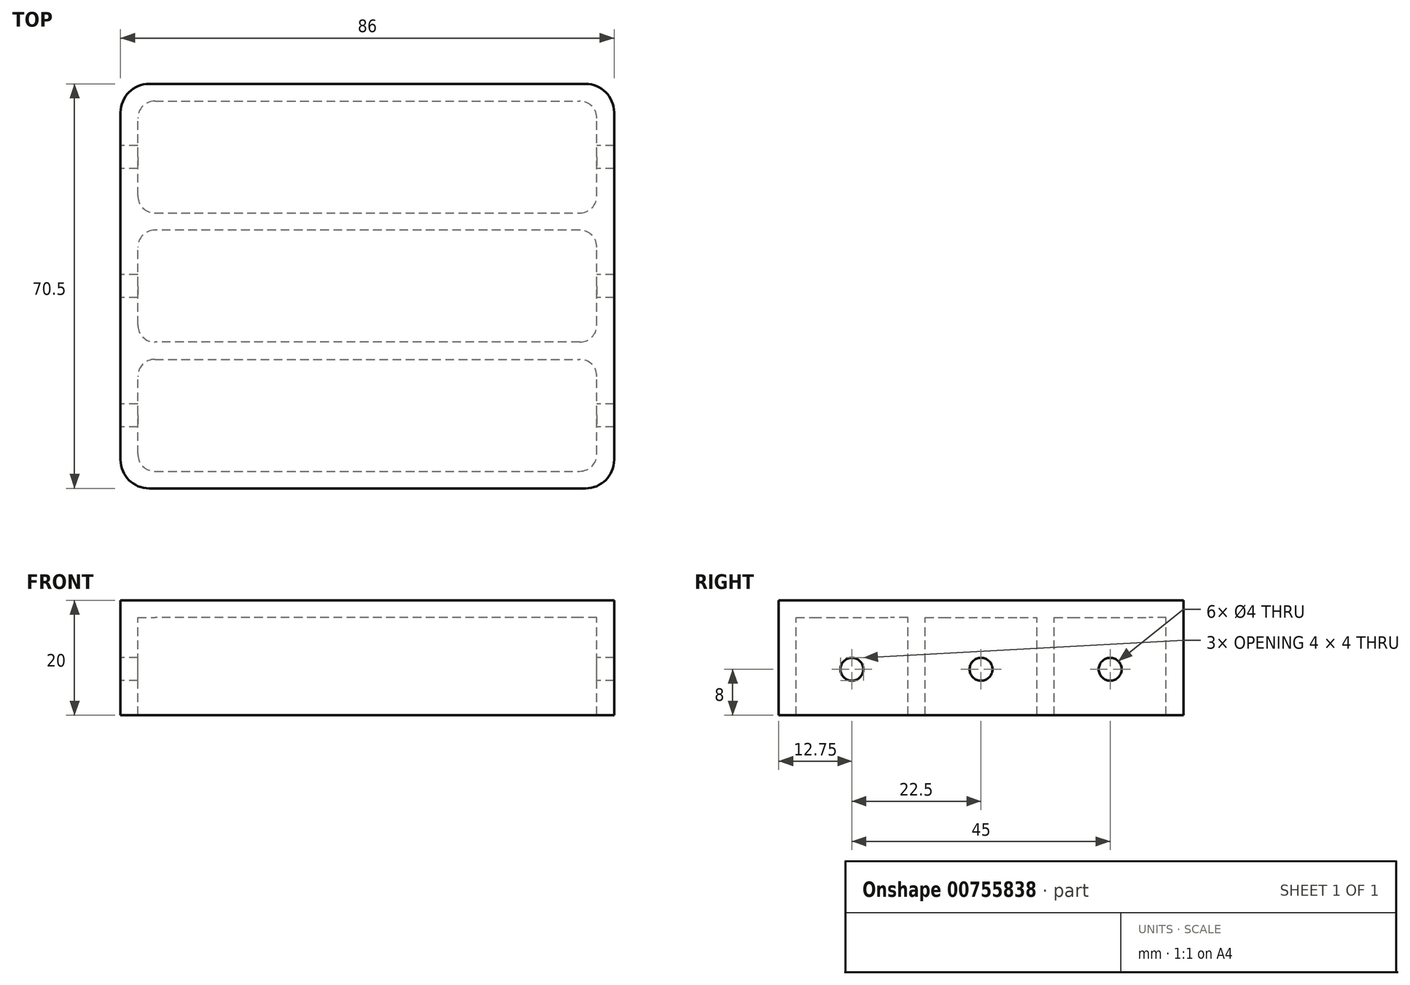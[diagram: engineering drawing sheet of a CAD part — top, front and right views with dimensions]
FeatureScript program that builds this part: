
annotation { "Feature Type Name" : "Feature", "Feature Type Description" : "" }
export const myFeature = defineFeature(function(context is Context, id is Id, definition is map)
    precondition{}
    {
        {
            var Q0;
            Q0=qCreatedBy(makeId("Top.planeOp"),FACE);
            var sketch = newSketch(context, id + "F0", { "sketchPlane" : qUnion([Q0])});
            skLineSegment(sketch, "E0.bottom", {"start": v(43, -35.25) * mm, "end": v(-43, -35.25) * mm});
            skLineSegment(sketch, "E0.top", {"start": v(43, 35.25) * mm, "end": v(-43, 35.25) * mm});
            skLineSegment(sketch, "E0.left", {"start": v(43, -35.25) * mm, "end": v(43, 35.25) * mm});
            skLineSegment(sketch, "E0.right", {"start": v(-43, -35.25) * mm, "end": v(-43, 35.25) * mm});
            skPoint(sketch, "E0.middle", {"position": v(0, 0) * mm});
            skLineSegment(sketch, "E1.bottom", {"start": v(40, -9.75) * mm, "end": v(-40, -9.75) * mm});
            skLineSegment(sketch, "E1.top", {"start": v(40, 9.75) * mm, "end": v(-40, 9.75) * mm});
            skLineSegment(sketch, "E1.left", {"start": v(40, -9.75) * mm, "end": v(40, 9.75) * mm});
            skLineSegment(sketch, "E1.right", {"start": v(-40, -9.75) * mm, "end": v(-40, 9.75) * mm});
            skLineSegment(sketch, "E2.bottom", {"start": v(-40, 12.75) * mm, "end": v(40, 12.75) * mm});
            skLineSegment(sketch, "E2.top", {"start": v(-40, 32.25) * mm, "end": v(40, 32.25) * mm});
            skLineSegment(sketch, "E2.left", {"start": v(-40, 12.75) * mm, "end": v(-40, 32.25) * mm});
            skLineSegment(sketch, "E2.right", {"start": v(40, 12.75) * mm, "end": v(40, 32.25) * mm});
            skPoint(sketch, "E2.middle", {"position": v(0, 22.5) * mm});
            skLineSegment(sketch, "E3.bottom", {"start": v(-40, -32.25) * mm, "end": v(40, -32.25) * mm});
            skLineSegment(sketch, "E3.top", {"start": v(-40, -12.75) * mm, "end": v(40, -12.75) * mm});
            skLineSegment(sketch, "E3.left", {"start": v(-40, -32.25) * mm, "end": v(-40, -12.75) * mm});
            skLineSegment(sketch, "E3.right", {"start": v(40, -32.25) * mm, "end": v(40, -12.75) * mm});
            skPoint(sketch, "E3.middle", {"position": v(0, -22.5) * mm});
            skSolve(sketch);
        }
        {
            var Q0;
            Q0=makeQuery(id+"F0.imprint","IMPRINT",FACE,{"disambiguationData":[TD([[makeQuery(id+"F0.imprint","IMPRINT",EDGE,{"derivedFrom":sQuery(id+"F0.wireOp",EDGE,"E0.bottom")}),-1.0]])]});
            var Q1;
            Q1=makeQuery(id+"F0.imprint","IMPRINT",FACE,{"disambiguationData":[TD([[makeQuery(id+"F0.imprint","IMPRINT",EDGE,{"derivedFrom":sQuery(id+"F0.wireOp",EDGE,"E3.bottom")}),1.0]])]});
            var Q2;
            Q2=makeQuery(id+"F0.imprint","IMPRINT",FACE,{"disambiguationData":[TD([[makeQuery(id+"F0.imprint","IMPRINT",EDGE,{"derivedFrom":sQuery(id+"F0.wireOp",EDGE,"E1.bottom")}),-1.0]])]});
            var Q3;
            Q3=makeQuery(id+"F0.imprint","IMPRINT",FACE,{"disambiguationData":[TD([[makeQuery(id+"F0.imprint","IMPRINT",EDGE,{"derivedFrom":sQuery(id+"F0.wireOp",EDGE,"E2.bottom")}),1.0]])]});
            extrude(context, id + "F1", {"entities" : qUnion([Q0, Q1, Q2, Q3]), "depth" : 3 * mm, "offsetDistance" : 25 * mm});
        }
        {
            var Q0;
            Q0 = qSketchRegion(id + "F0", true);
            extrude(context, id + "F2", {"entities" : qUnion([Q0]), "operationType" : NewBodyOperationType.ADD, "oppositeDirection" : true, "depth" : 17 * mm, "offsetDistance" : 25 * mm});
        }
        {
            var Q0;
            {var subQ0=sQuery(id+"F0.wireOp",EDGE,"E0.right");Q0=makeQuery(id+"F2.boolean.opBoolean","MERGE",FACE,{"derivedFrom":[makeQuery(id+"F1.opExtrude","SWEPT_FACE",FACE,{"disambiguationData":[OSD([subQ0])]}),makeQuery(id+"F2.opExtrude","SWEPT_FACE",FACE,{"disambiguationData":[OSD([subQ0])]})]});}
            var sketch = newSketch(context, id + "F3", { "sketchPlane" : qUnion([Q0])});
            skCircle(sketch, "E4", {"center": v(0, -9) * mm, "radius": 2 * mm});
            skPoint(sketch, "E4.centerSnap0", {"position": v(-35.25, -9) * mm});
            skCircle(sketch, "E5", {"center": v(-22.5, -9) * mm, "radius": 2 * mm});
            skCircle(sketch, "E6", {"center": v(22.5, -9) * mm, "radius": 2 * mm});
            skSolve(sketch);
        }
        {
            var Q0;
            Q0=sQuery(id+"F3.wireOp",VERTEX,"E5.center");
            var Q1;
            Q1=sQuery(id+"F3.wireOp",VERTEX,"E4.center");
            var Q2;
            Q2=sQuery(id+"F3.wireOp",VERTEX,"E6.center");
            var Q3;
            Q3=makeQuery(id+"F1.opExtrude","SWEPT_BODY",BODY,{"disambiguationData":[OSD([sQuery(id+"F0.wireOp",EDGE,"E0.bottom"),sQuery(id+"F0.wireOp",EDGE,"E0.top"),sQuery(id+"F0.wireOp",EDGE,"E0.left"),sQuery(id+"F0.wireOp",EDGE,"E0.right")])]});
            hole(context, id + "F4", {"style" : HoleStyle.SIMPLE, "endStyle" : HoleEndStyle.THROUGH, "holeDiameter" : 4 * mm, "majorDiameter" : 5 * mm, "isTappedThrough" : true, "tappedDepth" : 12 * mm, "tapClearance" : 3, "locations" : qUnion([Q0, Q1, Q2]), "scope" : qUnion([Q3])});
        }
        {
            var Q0;
            Q0=makeQuery(id+"F2.opExtrude","SWEPT_EDGE",EDGE,{"disambiguationData":[OSD([sQuery(id+"F0.wireOp",EDGE,"E2.top"),sQuery(id+"F0.wireOp",EDGE,"E2.right")])]});
            var Q1;
            Q1=makeQuery(id+"F2.opExtrude","SWEPT_EDGE",EDGE,{"disambiguationData":[OSD([sQuery(id+"F0.wireOp",EDGE,"E2.top"),sQuery(id+"F0.wireOp",EDGE,"E2.left")])]});
            var Q2;
            Q2=makeQuery(id+"F2.opExtrude","SWEPT_EDGE",EDGE,{"disambiguationData":[OSD([sQuery(id+"F0.wireOp",EDGE,"E2.bottom"),sQuery(id+"F0.wireOp",EDGE,"E2.left")])]});
            var Q3;
            Q3=makeQuery(id+"F2.opExtrude","SWEPT_EDGE",EDGE,{"disambiguationData":[OSD([sQuery(id+"F0.wireOp",EDGE,"E2.bottom"),sQuery(id+"F0.wireOp",EDGE,"E2.right")])]});
            var Q4;
            Q4=makeQuery(id+"F2.opExtrude","SWEPT_EDGE",EDGE,{"disambiguationData":[OSD([sQuery(id+"F0.wireOp",EDGE,"E1.bottom"),sQuery(id+"F0.wireOp",EDGE,"E1.left")])]});
            var Q5;
            Q5=makeQuery(id+"F2.opExtrude","SWEPT_EDGE",EDGE,{"disambiguationData":[OSD([sQuery(id+"F0.wireOp",EDGE,"E1.bottom"),sQuery(id+"F0.wireOp",EDGE,"E1.right")])]});
            var Q6;
            Q6=makeQuery(id+"F2.opExtrude","SWEPT_EDGE",EDGE,{"disambiguationData":[OSD([sQuery(id+"F0.wireOp",EDGE,"E1.top"),sQuery(id+"F0.wireOp",EDGE,"E1.right")])]});
            var Q7;
            Q7=makeQuery(id+"F2.opExtrude","SWEPT_EDGE",EDGE,{"disambiguationData":[OSD([sQuery(id+"F0.wireOp",EDGE,"E1.top"),sQuery(id+"F0.wireOp",EDGE,"E1.left")])]});
            var Q8;
            Q8=makeQuery(id+"F2.opExtrude","SWEPT_EDGE",EDGE,{"disambiguationData":[OSD([sQuery(id+"F0.wireOp",EDGE,"E3.top"),sQuery(id+"F0.wireOp",EDGE,"E3.right")])]});
            var Q9;
            Q9=makeQuery(id+"F2.opExtrude","SWEPT_EDGE",EDGE,{"disambiguationData":[OSD([sQuery(id+"F0.wireOp",EDGE,"E3.top"),sQuery(id+"F0.wireOp",EDGE,"E3.left")])]});
            var Q10;
            Q10=makeQuery(id+"F2.opExtrude","SWEPT_EDGE",EDGE,{"disambiguationData":[OSD([sQuery(id+"F0.wireOp",EDGE,"E3.bottom"),sQuery(id+"F0.wireOp",EDGE,"E3.left")])]});
            var Q11;
            Q11=makeQuery(id+"F2.opExtrude","SWEPT_EDGE",EDGE,{"disambiguationData":[OSD([sQuery(id+"F0.wireOp",EDGE,"E3.bottom"),sQuery(id+"F0.wireOp",EDGE,"E3.right")])]});
            fillet(context, id + "F5", {"entities" : qUnion([Q0, Q1, Q2, Q3, Q4, Q5, Q6, Q7, Q8, Q9, Q10, Q11]), "radius" : 3 * mm, "tangentPropagation" : true, "allowEdgeOverflow" : false});
        }
        {
            var Q0;
            {var subQ0=sQuery(id+"F0.wireOp",EDGE,"E0.left");var subQ1=sQuery(id+"F0.wireOp",EDGE,"E0.top");Q0=makeQuery(id+"F2.boolean.opBoolean","MERGE",EDGE,{"derivedFrom":[makeQuery(id+"F1.opExtrude","SWEPT_EDGE",EDGE,{"disambiguationData":[OSD([subQ1,subQ0])]}),makeQuery(id+"F2.opExtrude","SWEPT_EDGE",EDGE,{"disambiguationData":[OSD([subQ1,subQ0])]})]});}
            var Q1;
            {var subQ0=sQuery(id+"F0.wireOp",EDGE,"E0.left");var subQ1=sQuery(id+"F0.wireOp",EDGE,"E0.bottom");Q1=makeQuery(id+"F2.boolean.opBoolean","MERGE",EDGE,{"derivedFrom":[makeQuery(id+"F1.opExtrude","SWEPT_EDGE",EDGE,{"disambiguationData":[OSD([subQ1,subQ0])]}),makeQuery(id+"F2.opExtrude","SWEPT_EDGE",EDGE,{"disambiguationData":[OSD([subQ1,subQ0])]})]});}
            var Q2;
            {var subQ0=sQuery(id+"F0.wireOp",EDGE,"E0.right");var subQ1=sQuery(id+"F0.wireOp",EDGE,"E0.bottom");Q2=makeQuery(id+"F2.boolean.opBoolean","MERGE",EDGE,{"derivedFrom":[makeQuery(id+"F1.opExtrude","SWEPT_EDGE",EDGE,{"disambiguationData":[OSD([subQ1,subQ0])]}),makeQuery(id+"F2.opExtrude","SWEPT_EDGE",EDGE,{"disambiguationData":[OSD([subQ1,subQ0])]})]});}
            var Q3;
            {var subQ0=sQuery(id+"F0.wireOp",EDGE,"E0.right");var subQ1=sQuery(id+"F0.wireOp",EDGE,"E0.top");Q3=makeQuery(id+"F2.boolean.opBoolean","MERGE",EDGE,{"derivedFrom":[makeQuery(id+"F1.opExtrude","SWEPT_EDGE",EDGE,{"disambiguationData":[OSD([subQ1,subQ0])]}),makeQuery(id+"F2.opExtrude","SWEPT_EDGE",EDGE,{"disambiguationData":[OSD([subQ1,subQ0])]})]});}
            fillet(context, id + "F6", {"entities" : qUnion([Q0, Q1, Q2, Q3]), "radius" : 5 * mm, "tangentPropagation" : true, "allowEdgeOverflow" : false});
        }
    });
